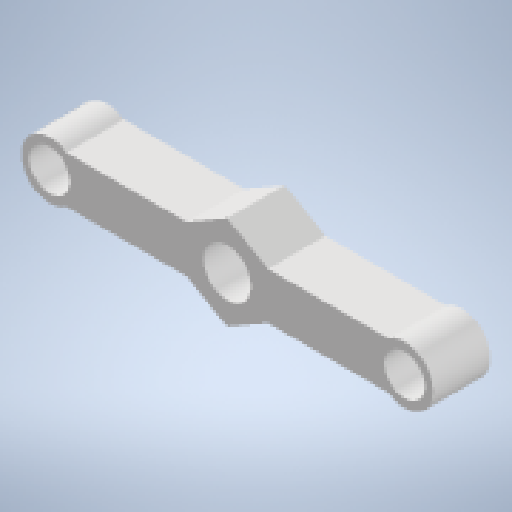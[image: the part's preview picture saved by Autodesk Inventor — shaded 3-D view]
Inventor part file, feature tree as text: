
AUTODESK INVENTOR PART (.ipt)
format: ipt  version: 2023 (Build 270158000, 158)  size: 162,816 bytes
history: native  units: mm
features: extrude x2, reference x2, sketch x1, other x1
ambient origin geometry x8: Origin, YZ Plane, XZ Plane, XY Plane, X Axis, Y Axis, Z Axis, Center Point
bodies: Solid1 (feature_tree)
feature tree (6):
  sketch  "Sketch1"  dims[d0=2.0mm d1=0.0mm d2=10.0mm d3=0.0mm]
  extrude  "Extrusion1"  Depth=10.0mm TaperAngle=0.0deg
  extrude  "Extrusion2"  [1 undecoded]
  reference  "Reference1"
  reference  "Reference2"
  other  "3D_skenner.iam"
note: 1 required parameter value undecoded (feature->parameter linkage not recoverable at this tier; creation-order binding heuristic only, values carry confidence <= 0.55)
